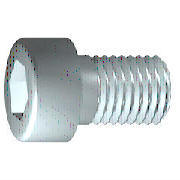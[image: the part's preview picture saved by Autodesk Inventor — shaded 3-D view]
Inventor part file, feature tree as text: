
AUTODESK INVENTOR PART (.ipt)
format: ipt  version: 2016 SP1 (Build 200210100, 210)  size: 195,584 bytes
history: native  units: mm (DEFAULTED — no unit token found)
features: sketch x2, extrude x1, plane x1, fillet x1
ambient origin geometry x7: Origin, YZ Plane, XY Plane, X Axis, Y Axis, Z Axis, Center Point
bodies: Solid1 (feature_tree), Body (feature_tree)
feature tree (5):
  extrude  "Slot"  Depth=2.0mm
  plane  "Work Plane1"
  fillet  "Fillet2"  Radius=2.0mm
  sketch  "Sketch1"  dims[d1=5.0mm d2=0.24548mm d3=2.0mm]
  sketch  "Sketch2"  dims[d4=1.0mm d5=60.0deg d6=2.0mm d7=2.0mm d8=1.732051mm d9=3.8mm d10=90.0deg d11=10.0mm d12=0.0mm d13=5.0mm d14=0.0mm d15=0.24538mm d16=0.24538mm d17=0.2mm d19=0.0mm d26=6.0mm d27=45.0deg d28=0.0mm d29=0.0mm d30=0.1mm]
